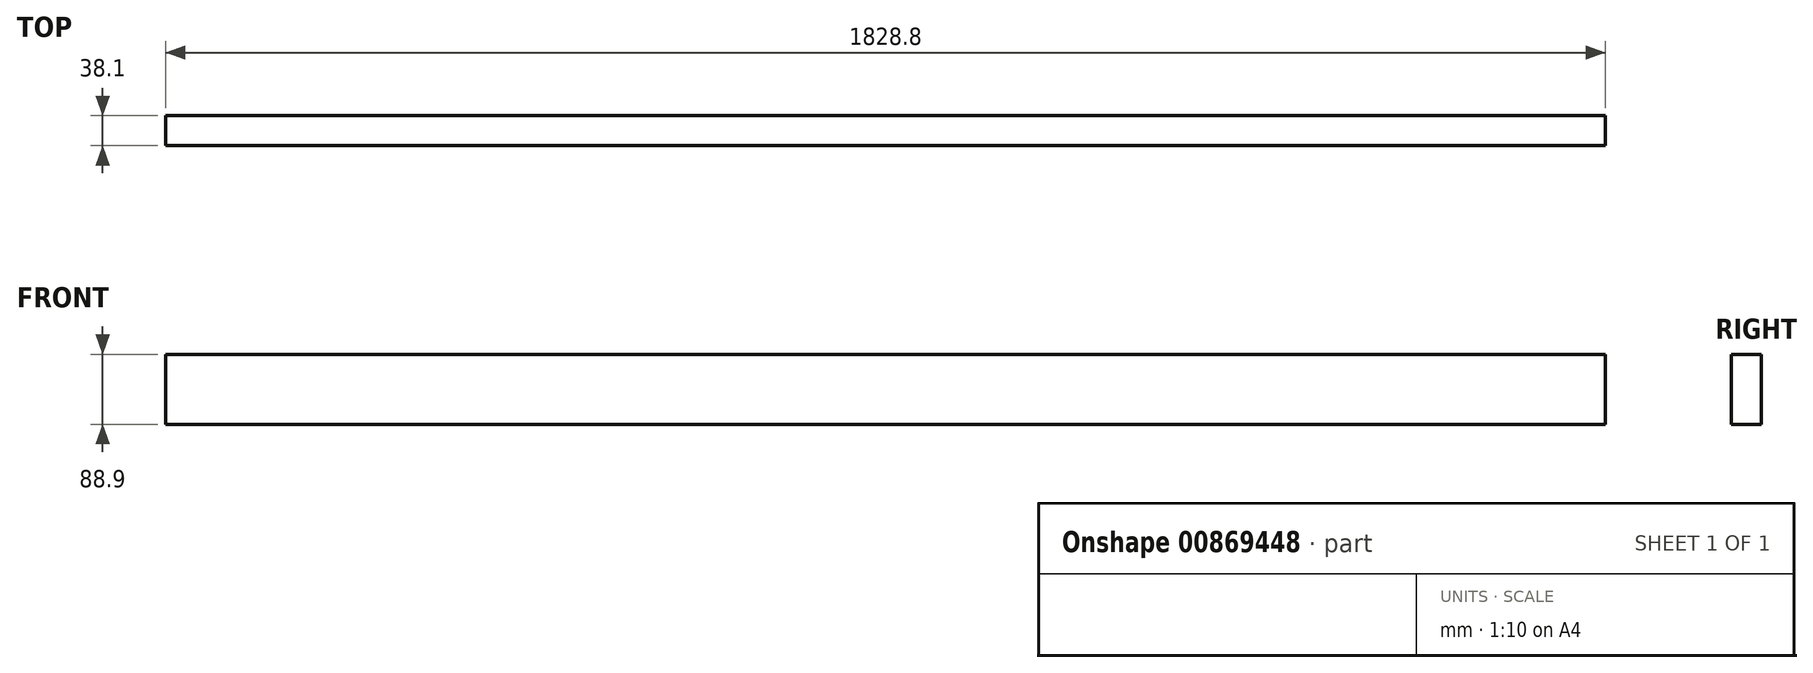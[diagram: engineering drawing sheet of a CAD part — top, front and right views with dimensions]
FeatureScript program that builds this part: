
annotation { "Feature Type Name" : "Feature", "Feature Type Description" : "" }
export const myFeature = defineFeature(function(context is Context, id is Id, definition is map)
    precondition{}
    {
        {
            var Q0;
            Q0=qCreatedBy(makeId("Front.planeOp"),FACE);
            var sketch = newSketch(context, id + "F0", { "sketchPlane" : qUnion([Q0])});
            skLineSegment(sketch, "E0", {"start": v(-61.6, 0) * mm, "end": v(1767.2, 0) * mm});
            skLineSegment(sketch, "E1", {"start": v(1767.2, 0) * mm, "end": v(1767.2, -88.9) * mm});
            skLineSegment(sketch, "E2", {"start": v(1767.2, -88.9) * mm, "end": v(-61.6, -88.9) * mm});
            skLineSegment(sketch, "E3", {"start": v(-61.6, -88.9) * mm, "end": v(-61.6, 0) * mm});
            skSolve(sketch);
        }
        {
            var Q0;
            Q0=makeQuery(id+"F0.imprint","IMPRINT",FACE,{"disambiguationData":[TD([[makeQuery(id+"F0.imprint","IMPRINT",EDGE,{"derivedFrom":sQuery(id+"F0.wireOp",EDGE,"E0")}),-1.0]])]});
            extrude(context, id + "F1", {"entities" : qUnion([Q0]), "depth" : 38.1 * mm, "offsetDistance" : 25.4 * mm});
        }
    });
